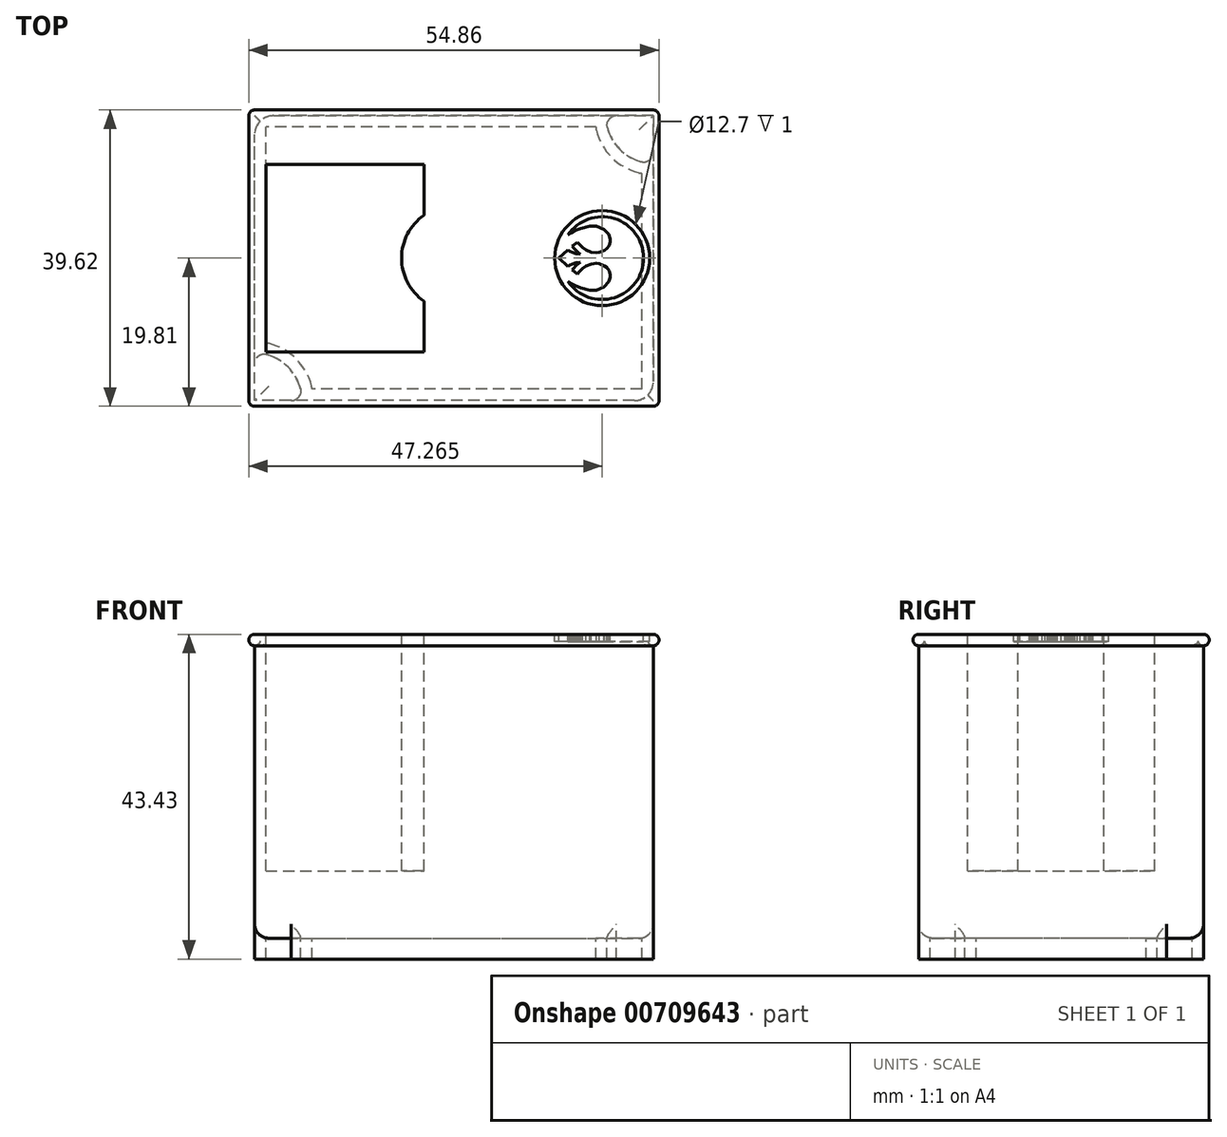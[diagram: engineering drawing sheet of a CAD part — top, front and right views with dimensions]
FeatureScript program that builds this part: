
annotation { "Feature Type Name" : "Feature", "Feature Type Description" : "" }
export const myFeature = defineFeature(function(context is Context, id is Id, definition is map)
    precondition{}
    {
        {
            var Q0;
            Q0=qCreatedBy(makeId("Front.planeOp"),FACE);
            var sketch = newSketch(context, id + "F0", { "sketchPlane" : qUnion([Q0])});
            skLineSegment(sketch, "E0.bottom", {"start": v(26.67, -20.32) * mm, "end": v(-26.67, -20.32) * mm});
            skLineSegment(sketch, "E0.top", {"start": v(26.67, 20.32) * mm, "end": v(-26.67, 20.32) * mm});
            skLineSegment(sketch, "E0.left", {"start": v(26.67, -20.32) * mm, "end": v(26.67, 20.32) * mm});
            skLineSegment(sketch, "E0.right", {"start": v(-26.67, -20.32) * mm, "end": v(-26.67, 20.32) * mm});
            skPoint(sketch, "E0.middle", {"position": v(0, 0) * mm});
            skSolve(sketch);
        }
        {
            var Q0;
            Q0=makeQuery(id+"F0.imprint","IMPRINT",FACE,{"disambiguationData":[TD([[makeQuery(id+"F0.imprint","IMPRINT",EDGE,{"derivedFrom":sQuery(id+"F0.wireOp",EDGE,"E0.bottom")}),-1.0]])]});
            extrude(context, id + "F1", {"entities" : qUnion([Q0]), "depth" : 38.1 * mm, "symmetric" : true});
        }
        {
            var Q0;
            Q0=makeQuery(id+"F1.opExtrude","SWEPT_FACE",FACE,{"disambiguationData":[OSD([sQuery(id+"F0.wireOp",EDGE,"E0.top")])]});
            shell(context, id + "F2", {"entities" : qUnion([Q0]), "thickness" : 1.52 * mm});
        }
        {
            var Q0;
            Q0=makeQuery(id+"F1.opExtrude","CAP_FACE",FACE,{"disambiguationData":[OSD([sQuery(id+"F0.wireOp",EDGE,"E0.bottom"),sQuery(id+"F0.wireOp",EDGE,"E0.top"),sQuery(id+"F0.wireOp",EDGE,"E0.left"),sQuery(id+"F0.wireOp",EDGE,"E0.right")])],"isStart":false});
            var sketch = newSketch(context, id + "F3", { "sketchPlane" : qUnion([Q0])});
            skArc(sketch, "E1", {"start": v(-26.67, 20.32) * mm, "mid": v(-27.43, 19.56) * mm, "end": v(-26.67, 18.8) * mm});
            skSolve(sketch);
        }
        {
            var Q0;
            {var subQ0=sQuery(id+"F3.wireOp",EDGE,"E1");Q0=makeQuery(id+"F3.imprint","IMPRINT",FACE,{"disambiguationData":[TD([[makeQuery(id+"F3.imprint","IMPRINT",EDGE,{"derivedFrom":subQ0}),1.0]])]});}
            var Q1;
            Q1=makeQuery(id+"F1.opExtrude","SWEPT_EDGE",EDGE,{"disambiguationData":[OSD([sQuery(id+"F0.wireOp",EDGE,"E0.top"),sQuery(id+"F0.wireOp",EDGE,"E0.right")])]});
            var Q2;
            Q2=makeQuery(id+"F1.opExtrude","CAP_EDGE",EDGE,{"disambiguationData":[OSD([sQuery(id+"F0.wireOp",EDGE,"E0.top")])],"isStart":true});
            var Q3;
            Q3=makeQuery(id+"F1.opExtrude","SWEPT_EDGE",EDGE,{"disambiguationData":[OSD([sQuery(id+"F0.wireOp",EDGE,"E0.top"),sQuery(id+"F0.wireOp",EDGE,"E0.left")])]});
            var Q4;
            Q4=makeQuery(id+"F1.opExtrude","CAP_EDGE",EDGE,{"disambiguationData":[OSD([sQuery(id+"F0.wireOp",EDGE,"E0.top")])],"isStart":false});
            sweep(context, id + "F4", {"operationType" : NewBodyOperationType.ADD, "profiles" : qUnion([Q0]), "path" : qUnion([Q1, Q2, Q3, Q4])});
        }
        {
            var Q0;
            Q0=makeQuery(id+"F1.opExtrude","SWEPT_FACE",FACE,{"disambiguationData":[OSD([sQuery(id+"F0.wireOp",EDGE,"E0.bottom")])]});
            var sketch = newSketch(context, id + "F5", { "sketchPlane" : qUnion([Q0])});
            skLineSegment(sketch, "E2.bottom", {"start": v(26.67, 19.05) * mm, "end": v(21.75, 19.05) * mm});
            skLineSegment(sketch, "E2.left", {"start": v(26.67, 19.05) * mm, "end": v(26.67, 14.13) * mm});
            skPoint(sketch, "E3.newPointA", {"position": v(20.32, 19.05) * mm});
            skArc(sketch, "E4", {"start": v(20.52, 17.46) * mm, "mid": v(22.18, 14.56) * mm, "end": v(25.08, 12.9) * mm});
            skArc(sketch, "E5.filletArc", {"start": v(21.75, 19.05) * mm, "mid": v(20.75, 18.56) * mm, "end": v(20.52, 17.46) * mm});
            skPoint(sketch, "E6.visualSharp", {"position": v(26.67, 12.7) * mm});
            skArc(sketch, "E6.filletArc", {"start": v(25.08, 12.9) * mm, "mid": v(26.18, 13.13) * mm, "end": v(26.67, 14.13) * mm});
            skArc(sketch, "E7.MirrorCS", {"start": v(-21.75, 19.05) * mm, "mid": v(-20.75, 18.56) * mm, "end": v(-20.52, 17.46) * mm});
            skArc(sketch, "E8.MirrorCS", {"start": v(-20.52, 17.46) * mm, "mid": v(-22.18, 14.56) * mm, "end": v(-25.08, 12.9) * mm});
            skArc(sketch, "E9.MirrorCS", {"start": v(-25.08, 12.9) * mm, "mid": v(-26.18, 13.13) * mm, "end": v(-26.67, 14.13) * mm});
            skLineSegment(sketch, "E10.MirrorCS", {"start": v(-26.67, 19.05) * mm, "end": v(-26.67, 14.13) * mm});
            skLineSegment(sketch, "E11.MirrorCS", {"start": v(-26.67, 19.05) * mm, "end": v(-21.75, 19.05) * mm});
            skArc(sketch, "E12.MirrorCS", {"start": v(-20.52, -17.46) * mm, "mid": v(-22.18, -14.56) * mm, "end": v(-25.08, -12.9) * mm});
            skArc(sketch, "E13.MirrorCS", {"start": v(-21.75, -19.05) * mm, "mid": v(-20.75, -18.56) * mm, "end": v(-20.52, -17.46) * mm});
            skLineSegment(sketch, "E14.MirrorCS", {"start": v(-26.67, -19.05) * mm, "end": v(-21.75, -19.05) * mm});
            skLineSegment(sketch, "E15.MirrorCS", {"start": v(-26.67, -19.05) * mm, "end": v(-26.67, -14.13) * mm});
            skArc(sketch, "E16.MirrorCS", {"start": v(-25.08, -12.9) * mm, "mid": v(-26.18, -13.13) * mm, "end": v(-26.67, -14.13) * mm});
            skArc(sketch, "E17.MirrorCS", {"start": v(21.75, -19.05) * mm, "mid": v(20.75, -18.56) * mm, "end": v(20.52, -17.46) * mm});
            skArc(sketch, "E18.MirrorCS", {"start": v(20.52, -17.46) * mm, "mid": v(22.18, -14.56) * mm, "end": v(25.08, -12.9) * mm});
            skArc(sketch, "E19.MirrorCS", {"start": v(25.08, -12.9) * mm, "mid": v(26.18, -13.13) * mm, "end": v(26.67, -14.13) * mm});
            skLineSegment(sketch, "E20.MirrorCS", {"start": v(26.67, -19.05) * mm, "end": v(26.67, -14.13) * mm});
            skLineSegment(sketch, "E21.MirrorCS", {"start": v(26.67, -19.05) * mm, "end": v(21.75, -19.05) * mm});
            skSolve(sketch);
        }
        {
            var Q0;
            Q0=makeQuery(id+"F5.imprint","IMPRINT",FACE,{"disambiguationData":[TD([[makeQuery(id+"F5.imprint","IMPRINT",EDGE,{"derivedFrom":sQuery(id+"F5.wireOp",EDGE,"E2.bottom")}),1.0]])]});
            var Q1;
            Q1=makeQuery(id+"F5.imprint","IMPRINT",FACE,{"disambiguationData":[TD([[makeQuery(id+"F5.imprint","IMPRINT",EDGE,{"derivedFrom":sQuery(id+"F5.wireOp",EDGE,"E8.MirrorCS")}),-1.0]])]});
            var Q2;
            Q2=makeQuery(id+"F5.imprint","IMPRINT",FACE,{"disambiguationData":[TD([[makeQuery(id+"F5.imprint","IMPRINT",EDGE,{"derivedFrom":sQuery(id+"F5.wireOp",EDGE,"E12.MirrorCS")}),1.0]])]});
            var Q3;
            Q3=makeQuery(id+"F5.imprint","IMPRINT",FACE,{"disambiguationData":[TD([[makeQuery(id+"F5.imprint","IMPRINT",EDGE,{"derivedFrom":sQuery(id+"F5.wireOp",EDGE,"E17.MirrorCS")}),-1.0]])]});
            extrude(context, id + "F6", {"entities" : qUnion([Q0, Q1, Q2, Q3]), "operationType" : NewBodyOperationType.ADD, "depth" : 2.8 * mm});
        }
        {
            var Q0;
            Q0=makeQuery(id+"F6.opExtrude","CAP_FACE",FACE,{"disambiguationData":[OSD([sQuery(id+"F5.wireOp",EDGE,"E2.bottom"),sQuery(id+"F5.wireOp",EDGE,"E2.left"),sQuery(id+"F5.wireOp",EDGE,"E4"),sQuery(id+"F5.wireOp",EDGE,"E5.filletArc"),sQuery(id+"F5.wireOp",EDGE,"E6.filletArc")])],"isStart":false});
            var Q1;
            Q1=makeQuery(id+"F6.opExtrude","CAP_FACE",FACE,{"disambiguationData":[OSD([sQuery(id+"F5.wireOp",EDGE,"E8.MirrorCS"),sQuery(id+"F5.wireOp",EDGE,"E9.MirrorCS"),sQuery(id+"F5.wireOp",EDGE,"E10.MirrorCS"),sQuery(id+"F5.wireOp",EDGE,"E7.MirrorCS"),sQuery(id+"F5.wireOp",EDGE,"E11.MirrorCS")])],"isStart":false});
            var Q2;
            Q2=makeQuery(id+"F6.opExtrude","CAP_FACE",FACE,{"disambiguationData":[OSD([sQuery(id+"F5.wireOp",EDGE,"E12.MirrorCS"),sQuery(id+"F5.wireOp",EDGE,"E13.MirrorCS"),sQuery(id+"F5.wireOp",EDGE,"E14.MirrorCS"),sQuery(id+"F5.wireOp",EDGE,"E15.MirrorCS"),sQuery(id+"F5.wireOp",EDGE,"E16.MirrorCS")])],"isStart":false});
            var Q3;
            Q3=makeQuery(id+"F6.opExtrude","CAP_FACE",FACE,{"disambiguationData":[OSD([sQuery(id+"F5.wireOp",EDGE,"E17.MirrorCS"),sQuery(id+"F5.wireOp",EDGE,"E18.MirrorCS"),sQuery(id+"F5.wireOp",EDGE,"E19.MirrorCS"),sQuery(id+"F5.wireOp",EDGE,"E20.MirrorCS"),sQuery(id+"F5.wireOp",EDGE,"E21.MirrorCS")])],"isStart":false});
            shell(context, id + "F7", {"entities" : qUnion([Q0, Q1, Q2, Q3]), "thickness" : 1.52 * mm});
        }
        {
            var Q0;
            Q0=makeQuery(id+"F2.opShell","OFFSET_FACE",FACE,{"disambiguationData":[OSD([sQuery(id+"F0.wireOp",EDGE,"E0.bottom")])]});
            extrude(context, id + "F8", {"entities" : qUnion([Q0]), "operationType" : NewBodyOperationType.ADD, "surfaceOperationType" : NewSurfaceOperationType.ADD, "depth" : 7.5 * mm, "offsetDistance" : 25 * mm});
        }
        {
            var Q0;
            Q0=makeQuery(id+"F1.opExtrude","SWEPT_EDGE",EDGE,{"disambiguationData":[OSD([sQuery(id+"F0.wireOp",EDGE,"E0.bottom"),sQuery(id+"F0.wireOp",EDGE,"E0.right")])]});
            var Q1;
            Q1=makeQuery(id+"F1.opExtrude","CAP_EDGE",EDGE,{"disambiguationData":[OSD([sQuery(id+"F0.wireOp",EDGE,"E0.bottom")])],"isStart":false});
            var Q2;
            Q2=makeQuery(id+"F1.opExtrude","SWEPT_EDGE",EDGE,{"disambiguationData":[OSD([sQuery(id+"F0.wireOp",EDGE,"E0.bottom"),sQuery(id+"F0.wireOp",EDGE,"E0.left")])]});
            var Q3;
            Q3=makeQuery(id+"F1.opExtrude","CAP_EDGE",EDGE,{"disambiguationData":[OSD([sQuery(id+"F0.wireOp",EDGE,"E0.bottom")])],"isStart":true});
            fillet(context, id + "F9", {"entities" : qUnion([Q0, Q1, Q2, Q3]), "radius" : 1.9 * mm, "tangentPropagation" : true, "allowEdgeOverflow" : false});
        }
        {
            var Q0;
            Q0=makeQuery(id+"F4.opSweep","MID_CAP_EDGE",EDGE,{"disambiguationData":[OSD([sQuery(id+"F0.wireOp",EDGE,"E0.top"),sQuery(id+"F0.wireOp",EDGE,"E0.left"),sQuery(id+"F3.wireOp",EDGE,"E1")])],"capPos":3.0});
            var Q1;
            Q1=makeQuery(id+"F4.opSweep","MID_CAP_EDGE",EDGE,{"disambiguationData":[OSD([sQuery(id+"F0.wireOp",EDGE,"E0.top"),sQuery(id+"F0.wireOp",EDGE,"E0.left"),sQuery(id+"F3.wireOp",EDGE,"E1")])],"capPos":2.0});
            var Q2;
            Q2=makeQuery(id+"F4.opSweep","MID_CAP_EDGE",EDGE,{"disambiguationData":[OSD([sQuery(id+"F0.wireOp",EDGE,"E0.top"),sQuery(id+"F0.wireOp",EDGE,"E0.right"),sQuery(id+"F3.wireOp",EDGE,"E1")])],"capPos":1.0});
            var Q3;
            Q3=makeQuery(id+"F4.opSweep","CAP_EDGE",EDGE,{"disambiguationData":[OSD([sQuery(id+"F0.wireOp",EDGE,"E0.top"),sQuery(id+"F0.wireOp",EDGE,"E0.right"),sQuery(id+"F3.wireOp",EDGE,"E1")])],"isStart":true});
            fillet(context, id + "F10", {"entities" : qUnion([Q0, Q1, Q2, Q3]), "radius" : 0.76 * mm, "tangentPropagation" : true, "allowEdgeOverflow" : false});
        }
        {
            var Q0;
            Q0=makeQuery(id+"F6.boolean.opBoolean","MERGE",EDGE,{"derivedFrom":[makeQuery(id+"F1.opExtrude","CAP_EDGE",EDGE,{"disambiguationData":[OSD([sQuery(id+"F0.wireOp",EDGE,"E0.left")])],"isStart":false}),makeQuery(id+"F6.opExtrude","SWEPT_EDGE",EDGE,{"disambiguationData":[OSD([sQuery(id+"F5.wireOp",EDGE,"E2.bottom"),sQuery(id+"F5.wireOp",EDGE,"E2.left")])]})]});
            var Q1;
            Q1=makeQuery(id+"F6.boolean.opBoolean","MERGE",EDGE,{"derivedFrom":[makeQuery(id+"F1.opExtrude","CAP_EDGE",EDGE,{"disambiguationData":[OSD([sQuery(id+"F0.wireOp",EDGE,"E0.left")])],"isStart":true}),makeQuery(id+"F6.opExtrude","SWEPT_EDGE",EDGE,{"disambiguationData":[OSD([sQuery(id+"F5.wireOp",EDGE,"E20.MirrorCS"),sQuery(id+"F5.wireOp",EDGE,"E21.MirrorCS")])]})]});
            var Q2;
            Q2=makeQuery(id+"F6.boolean.opBoolean","MERGE",EDGE,{"derivedFrom":[makeQuery(id+"F1.opExtrude","CAP_EDGE",EDGE,{"disambiguationData":[OSD([sQuery(id+"F0.wireOp",EDGE,"E0.right")])],"isStart":false}),makeQuery(id+"F6.opExtrude","SWEPT_EDGE",EDGE,{"disambiguationData":[OSD([sQuery(id+"F5.wireOp",EDGE,"E10.MirrorCS"),sQuery(id+"F5.wireOp",EDGE,"E11.MirrorCS")])]})]});
            var Q3;
            Q3=makeQuery(id+"F6.boolean.opBoolean","MERGE",EDGE,{"derivedFrom":[makeQuery(id+"F1.opExtrude","CAP_EDGE",EDGE,{"disambiguationData":[OSD([sQuery(id+"F0.wireOp",EDGE,"E0.right")])],"isStart":true}),makeQuery(id+"F6.opExtrude","SWEPT_EDGE",EDGE,{"disambiguationData":[OSD([sQuery(id+"F5.wireOp",EDGE,"E14.MirrorCS"),sQuery(id+"F5.wireOp",EDGE,"E15.MirrorCS")])]})]});
            fillet(context, id + "F11", {"entities" : qUnion([Q0, Q1, Q2, Q3]), "radius" : 2.54 * mm, "tangentPropagation" : true, "allowEdgeOverflow" : false});
        }
        {
            var Q0;
            Q0=makeQuery(id+"F1.opExtrude","SWEPT_FACE",FACE,{"disambiguationData":[OSD([sQuery(id+"F0.wireOp",EDGE,"E0.top")])]});
            var sketch = newSketch(context, id + "F12", { "sketchPlane" : qUnion([Q0])});
            skLineSegment(sketch, "E22.0", {"start": v(25.15, -17.53) * mm, "end": v(-25.15, -17.53) * mm});
            skLineSegment(sketch, "E22.1", {"start": v(-25.15, -17.53) * mm, "end": v(-25.15, 17.53) * mm});
            skLineSegment(sketch, "E22.2", {"start": v(25.15, 17.53) * mm, "end": v(-25.15, 17.53) * mm});
            skLineSegment(sketch, "E22.3", {"start": v(25.15, -17.53) * mm, "end": v(25.15, 17.53) * mm});
            skLineSegment(sketch, "E23", {"start": v(-25.15, 17.53) * mm, "end": v(-25.15, 12.53) * mm});
            skLineSegment(sketch, "E24", {"start": v(-25.15, 12.53) * mm, "end": v(-4, 12.53) * mm});
            skLineSegment(sketch, "E25", {"start": v(-25.15, -17.53) * mm, "end": v(-25.15, -12.53) * mm});
            skLineSegment(sketch, "E26", {"start": v(-25.15, -12.53) * mm, "end": v(-4, -12.53) * mm});
            skLineSegment(sketch, "E27.left", {"start": v(-4, 12.53) * mm, "end": v(-4, 5.74) * mm});
            skLineSegment(sketch, "E27.right", {"start": v(4, 12.53) * mm, "end": v(4, 5.74) * mm});
            skPoint(sketch, "E27.middle", {"position": v(0, 0) * mm});
            skArc(sketch, "E28", {"start": v(-4, 5.74) * mm, "mid": v(-7, 0) * mm, "end": v(-4, -5.74) * mm});
            skLineSegment(sketch, "E29.bottom", {"start": v(13, 2.25) * mm, "end": v(6.63, 2.25) * mm});
            skLineSegment(sketch, "E29.top", {"start": v(13, -2.25) * mm, "end": v(6.63, -2.25) * mm});
            skLineSegment(sketch, "E29.left", {"start": v(13, 2.25) * mm, "end": v(13, -2.25) * mm});
            skLineSegment(sketch, "E30.trimOffspring", {"start": v(4, -5.74) * mm, "end": v(4, -12.53) * mm});
            skLineSegment(sketch, "E31.trimOffspring", {"start": v(-4, -5.74) * mm, "end": v(-4, -12.53) * mm});
            skArc(sketch, "E32.trimOffspring", {"start": v(4, -5.74) * mm, "mid": v(5.6, -4.2) * mm, "end": v(6.63, -2.25) * mm});
            skLineSegment(sketch, "E33.trimOffspring", {"start": v(4, -12.53) * mm, "end": v(25.15, -12.53) * mm});
            skLineSegment(sketch, "E34.trimOffspring", {"start": v(4, 12.53) * mm, "end": v(25.15, 12.53) * mm});
            skArc(sketch, "E35.trimOffspring", {"start": v(6.63, 2.25) * mm, "mid": v(5.6, 4.2) * mm, "end": v(4, 5.74) * mm});
            skSolve(sketch);
        }
        {
            var Q0;
            Q0=makeQuery(id+"F12.imprint","IMPRINT",FACE,{"disambiguationData":[TD([[makeQuery(id+"F12.imprint","IMPRINT",EDGE,{"derivedFrom":sQuery(id+"F12.wireOp",EDGE,"E22.1")}),-1.0]])]});
            var Q1;
            Q1=makeQuery(id+"F12.imprint","IMPRINT",FACE,{"disambiguationData":[TD([[makeQuery(id+"F12.imprint","IMPRINT",EDGE,{"derivedFrom":sQuery(id+"F12.wireOp",EDGE,"E27.right")}),1.0]])]});
            var Q2;
            Q2=makeQuery(id+"F8.opExtrude","CAP_FACE",FACE,{"disambiguationData":[OSD([sQuery(id+"F0.wireOp",EDGE,"E0.bottom")])],"isStart":false});
            extrude(context, id + "F13", {"entities" : qUnion([Q0, Q1]), "operationType" : NewBodyOperationType.ADD, "endBound" : BoundingType.UP_TO_SURFACE, "oppositeDirection" : true, "depth" : 25 * mm, "endBoundEntityFace" : qUnion([Q2]), "offsetDistance" : 25 * mm});
        }
        {
            var Q0;
            {var subQ2=sQuery(id+"F0.wireOp",EDGE,"E0.top");var subQ4=sQuery(id+"F12.wireOp",EDGE,"E30.trimOffspring");var subQ5=sQuery(id+"F12.wireOp",EDGE,"E27.left");var subQ6=sQuery(id+"F0.wireOp",EDGE,"E0.left");var subQ7=sQuery(id+"F12.wireOp",EDGE,"E24");var subQ8=sQuery(id+"F12.wireOp",EDGE,"E26");var subQ9=sQuery(id+"F12.wireOp",EDGE,"E29.bottom");var subQ11=sQuery(id+"F12.wireOp",EDGE,"E28");var subQ12=sQuery(id+"F12.wireOp",EDGE,"E27.right");var subQ13=sQuery(id+"F12.wireOp",EDGE,"E29.left");var subQ14=sQuery(id+"F12.wireOp",EDGE,"E31.trimOffspring");var subQ15=sQuery(id+"F12.wireOp",EDGE,"E29.top");var subQ16=sQuery(id+"F12.wireOp",EDGE,"E32.trimOffspring");var subQ17=sQuery(id+"F12.wireOp",EDGE,"E33.trimOffspring");var subQ18=sQuery(id+"F12.wireOp",EDGE,"E34.trimOffspring");var subQ19=sQuery(id+"F12.wireOp",EDGE,"E35.trimOffspring");Q0=makeQuery(id+"F16.boolean.opBoolean","SPLIT",FACE,{"disambiguationData":[TD([makeQuery(id+"F2.opShell","OFFSET_FACE",FACE,{"disambiguationData":[OSD([subQ6])]})])],"derivedFrom":makeQuery(id+"F13.boolean.opBoolean","MERGE",FACE,{"derivedFrom":[makeQuery(id+"F1.opExtrude","SWEPT_FACE",FACE,{"disambiguationData":[OSD([subQ2])]}),makeQuery(id+"F13.opExtrude","CAP_FACE",FACE,{"disambiguationData":[OSD([sQuery(id+"F12.wireOp",EDGE,"E22.1"),subQ7,subQ8,subQ5,subQ11,subQ14])],"isStart":true}),makeQuery(id+"F13.opExtrude","CAP_FACE",FACE,{"disambiguationData":[OSD([sQuery(id+"F12.wireOp",EDGE,"E22.3"),subQ12,subQ9,subQ15,subQ13,subQ4,subQ16,subQ17,subQ18,subQ19])],"isStart":true})]})});}
            var sketch = newSketch(context, id + "F14", { "sketchPlane" : qUnion([Q0])});
            skCircle(sketch, "E36", {"center": v(19.84, 0) * mm, "radius": 6.35 * mm});
            skLineSegment(sketch, "E37", {"start": v(15.28, 1.1) * mm, "end": v(14.03, 0) * mm});
            skLineSegment(sketch, "E38", {"start": v(15.83, 1.6) * mm, "end": v(16.54, 2.14) * mm});
            skLineSegment(sketch, "E39", {"start": v(16.54, 2.14) * mm, "end": v(16.77, 1.84) * mm});
            skLineSegment(sketch, "E40", {"start": v(16.77, 1.84) * mm, "end": v(17.23, 1.4) * mm});
            skLineSegment(sketch, "E41", {"start": v(17.23, 1.4) * mm, "end": v(17.63, 1.08) * mm});
            skLineSegment(sketch, "E42", {"start": v(17.63, 1.08) * mm, "end": v(18.33, 0.77) * mm});
            skLineSegment(sketch, "E43", {"start": v(18.33, 0.77) * mm, "end": v(19.08, 0.7) * mm});
            skLineSegment(sketch, "E44", {"start": v(19.08, 0.7) * mm, "end": v(19.45, 0.76) * mm});
            skLineSegment(sketch, "E45", {"start": v(19.45, 0.76) * mm, "end": v(20.14, 1.07) * mm});
            skLineSegment(sketch, "E46", {"start": v(20.14, 1.07) * mm, "end": v(20.46, 1.27) * mm});
            skLineSegment(sketch, "E47", {"start": v(20.46, 1.27) * mm, "end": v(20.75, 1.7) * mm});
            skLineSegment(sketch, "E48", {"start": v(20.75, 1.7) * mm, "end": v(20.9, 2.19) * mm});
            skLineSegment(sketch, "E49", {"start": v(20.9, 2.19) * mm, "end": v(20.9, 2.56) * mm});
            skLineSegment(sketch, "E50", {"start": v(20.9, 2.56) * mm, "end": v(20.71, 3.18) * mm});
            skLineSegment(sketch, "E51", {"start": v(20.71, 3.18) * mm, "end": v(20.1, 3.83) * mm});
            skLineSegment(sketch, "E52", {"start": v(20.1, 3.83) * mm, "end": v(19.06, 4.28) * mm});
            skLineSegment(sketch, "E53", {"start": v(19.06, 4.28) * mm, "end": v(18.18, 4.28) * mm});
            skLineSegment(sketch, "E54", {"start": v(18.18, 4.28) * mm, "end": v(16.93, 3.99) * mm});
            skLineSegment(sketch, "E55", {"start": v(16.93, 3.99) * mm, "end": v(16.22, 3.69) * mm});
            skLineSegment(sketch, "E56", {"start": v(16.22, 3.69) * mm, "end": v(15.67, 3.4) * mm});
            skLineSegment(sketch, "E57", {"start": v(15.67, 3.4) * mm, "end": v(15.26, 3.1) * mm});
            skLineSegment(sketch, "E58", {"start": v(15.83, 1.6) * mm, "end": v(16, 1.38) * mm});
            skLineSegment(sketch, "E59", {"start": v(16, 1.38) * mm, "end": v(16.35, 1.02) * mm});
            skLineSegment(sketch, "E60", {"start": v(16.35, 1.02) * mm, "end": v(16.62, 0.74) * mm});
            skLineSegment(sketch, "E61", {"start": v(16.62, 0.74) * mm, "end": v(16.93, 0.53) * mm});
            skLineSegment(sketch, "E62", {"start": v(16.93, 0.53) * mm, "end": v(16.3, 0.62) * mm});
            skLineSegment(sketch, "E63", {"start": v(16.3, 0.62) * mm, "end": v(15.83, 0.78) * mm});
            skLineSegment(sketch, "E64", {"start": v(15.83, 0.78) * mm, "end": v(15.49, 0.93) * mm});
            skLineSegment(sketch, "E65", {"start": v(15.49, 0.93) * mm, "end": v(15.28, 1.1) * mm});
            skPoint(sketch, "E66.start.orphan", {"position": v(13.49, 0) * mm});
            skLineSegment(sketch, "E67.MirrorCS", {"start": v(20.46, -1.27) * mm, "end": v(20.75, -1.7) * mm});
            skLineSegment(sketch, "E68.MirrorCS", {"start": v(16.22, -3.69) * mm, "end": v(15.67, -3.4) * mm});
            skLineSegment(sketch, "E69.MirrorCS", {"start": v(20.14, -1.07) * mm, "end": v(20.46, -1.27) * mm});
            skLineSegment(sketch, "E70.MirrorCS", {"start": v(19.06, -4.28) * mm, "end": v(18.18, -4.28) * mm});
            skLineSegment(sketch, "E71.MirrorCS", {"start": v(16.93, -0.53) * mm, "end": v(16.3, -0.62) * mm});
            skLineSegment(sketch, "E72.MirrorCS", {"start": v(16.77, -1.84) * mm, "end": v(17.23, -1.4) * mm});
            skLineSegment(sketch, "E73.MirrorCS", {"start": v(16.3, -0.62) * mm, "end": v(15.83, -0.78) * mm});
            skLineSegment(sketch, "E74.MirrorCS", {"start": v(15.83, -0.78) * mm, "end": v(15.49, -0.93) * mm});
            skLineSegment(sketch, "E75.MirrorCS", {"start": v(16.62, -0.74) * mm, "end": v(16.93, -0.53) * mm});
            skLineSegment(sketch, "E76.MirrorCS", {"start": v(20.9, -2.56) * mm, "end": v(20.71, -3.18) * mm});
            skLineSegment(sketch, "E77.MirrorCS", {"start": v(20.71, -3.18) * mm, "end": v(20.1, -3.83) * mm});
            skLineSegment(sketch, "E78.MirrorCS", {"start": v(15.67, -3.4) * mm, "end": v(15.26, -3.1) * mm});
            skLineSegment(sketch, "E79.MirrorCS", {"start": v(16.93, -3.99) * mm, "end": v(16.22, -3.69) * mm});
            skLineSegment(sketch, "E80.MirrorCS", {"start": v(16, -1.38) * mm, "end": v(16.35, -1.02) * mm});
            skLineSegment(sketch, "E81.MirrorCS", {"start": v(17.23, -1.4) * mm, "end": v(17.63, -1.08) * mm});
            skLineSegment(sketch, "E82.MirrorCS", {"start": v(20.75, -1.7) * mm, "end": v(20.9, -2.19) * mm});
            skLineSegment(sketch, "E83.MirrorCS", {"start": v(16.54, -2.14) * mm, "end": v(16.77, -1.84) * mm});
            skLineSegment(sketch, "E84.MirrorCS", {"start": v(15.83, -1.6) * mm, "end": v(16, -1.38) * mm});
            skLineSegment(sketch, "E85.MirrorCS", {"start": v(19.45, -0.76) * mm, "end": v(20.14, -1.07) * mm});
            skLineSegment(sketch, "E86.MirrorCS", {"start": v(15.83, -1.6) * mm, "end": v(16.54, -2.14) * mm});
            skLineSegment(sketch, "E87.MirrorCS", {"start": v(19.08, -0.7) * mm, "end": v(19.45, -0.76) * mm});
            skLineSegment(sketch, "E88.MirrorCS", {"start": v(17.63, -1.08) * mm, "end": v(18.33, -0.77) * mm});
            skLineSegment(sketch, "E89.MirrorCS", {"start": v(18.33, -0.77) * mm, "end": v(19.08, -0.7) * mm});
            skLineSegment(sketch, "E90.MirrorCS", {"start": v(16.35, -1.02) * mm, "end": v(16.62, -0.74) * mm});
            skLineSegment(sketch, "E91.MirrorCS", {"start": v(15.49, -0.93) * mm, "end": v(15.28, -1.1) * mm});
            skLineSegment(sketch, "E92.MirrorCS", {"start": v(20.9, -2.19) * mm, "end": v(20.9, -2.56) * mm});
            skLineSegment(sketch, "E93.MirrorCS", {"start": v(18.18, -4.28) * mm, "end": v(16.93, -3.99) * mm});
            skLineSegment(sketch, "E94.MirrorCS", {"start": v(15.28, -1.1) * mm, "end": v(14.03, 0) * mm});
            skLineSegment(sketch, "E95.MirrorCS", {"start": v(20.1, -3.83) * mm, "end": v(19.06, -4.28) * mm});
            skArc(sketch, "E96", {"start": v(15.26, -3.1) * mm, "mid": v(25.37, 0) * mm, "end": v(15.26, 3.1) * mm});
            skPoint(sketch, "E97", {"position": v(19.83, 0) * mm});
            skPoint(sketch, "E98", {"position": v(19.84, 6.35) * mm});
            skPoint(sketch, "E99.0", {"position": v(13, 0) * mm});
            skPoint(sketch, "E100.0", {"position": v(26.67, 0) * mm});
            skSolve(sketch);
        }
        {
            var Q0;
            Q0=makeQuery(id+"F13.boolean.opBoolean","MERGE",FACE,{"derivedFrom":[makeQuery(id+"F1.opExtrude","SWEPT_FACE",FACE,{"disambiguationData":[OSD([sQuery(id+"F0.wireOp",EDGE,"E0.top")])]}),makeQuery(id+"F13.opExtrude","CAP_FACE",FACE,{"disambiguationData":[OSD([sQuery(id+"F12.wireOp",EDGE,"E22.1"),sQuery(id+"F12.wireOp",EDGE,"E24"),sQuery(id+"F12.wireOp",EDGE,"E26"),sQuery(id+"F12.wireOp",EDGE,"E27.left"),sQuery(id+"F12.wireOp",EDGE,"E28"),sQuery(id+"F12.wireOp",EDGE,"E31.trimOffspring")])],"isStart":true}),makeQuery(id+"F13.opExtrude","CAP_FACE",FACE,{"disambiguationData":[OSD([sQuery(id+"F12.wireOp",EDGE,"E22.3"),sQuery(id+"F12.wireOp",EDGE,"E27.right"),sQuery(id+"F12.wireOp",EDGE,"E29.bottom"),sQuery(id+"F12.wireOp",EDGE,"E29.top"),sQuery(id+"F12.wireOp",EDGE,"E29.left"),sQuery(id+"F12.wireOp",EDGE,"E30.trimOffspring"),sQuery(id+"F12.wireOp",EDGE,"E32.trimOffspring"),sQuery(id+"F12.wireOp",EDGE,"E33.trimOffspring"),sQuery(id+"F12.wireOp",EDGE,"E34.trimOffspring"),sQuery(id+"F12.wireOp",EDGE,"E35.trimOffspring")])],"isStart":true})]});
            var sketch = newSketch(context, id + "F15", { "sketchPlane" : qUnion([Q0])});
            skPoint(sketch, "E101.0", {"position": v(-22.16, -12.53) * mm});
            skPoint(sketch, "E102", {"position": v(-18.34, -11.53) * mm});
            skLineSegment(sketch, "E103", {"start": v(-13.8, 0) * mm, "end": v(-12.37, 0) * mm});
            skPoint(sketch, "E104", {"position": v(-12.37, -11.53) * mm});
            skPoint(sketch, "E105", {"position": v(-12.37, 11.53) * mm});
            skPoint(sketch, "E106", {"position": v(-13.8, 11.53) * mm});
            skPoint(sketch, "E107", {"position": v(-13.8, -11.53) * mm});
            skPoint(sketch, "E108", {"position": v(-18.34, 11.53) * mm});
            skPoint(sketch, "E109", {"position": v(-7.84, -11.53) * mm});
            skPoint(sketch, "E110", {"position": v(-7.84, 11.53) * mm});
            skText(sketch, "E111", { "text": "Fighter", "fontName": "NotoSans-Bold.ttf"});
            skPoint(sketch, "E112", {"position": v(-18.34, 0) * mm});
            skText(sketch, "E113", { "text": "TIE", "fontName": "NotoSans-Bold.ttf"});
            skPoint(sketch, "E114.0", {"position": v(-4, 12.53) * mm});
            skLineSegment(sketch, "E115.0", {"start": v(-25.15, 12.53) * mm, "end": v(-7, 12.53) * mm});
            skPoint(sketch, "E116.0", {"position": v(-4.02, 0) * mm});
            skPoint(sketch, "E117.0", {"position": v(-22.37, 50.53) * mm});
            skPoint(sketch, "E118.0", {"position": v(-19.55, 75.58) * mm});
            skPoint(sketch, "E119", {"position": v(-18.55, 51.53) * mm});
            skLineSegment(sketch, "E120", {"start": v(-14.02, 63.06) * mm, "end": v(-12.58, 63.06) * mm});
            skPoint(sketch, "E121", {"position": v(-12.58, 51.53) * mm});
            skPoint(sketch, "E122", {"position": v(-12.58, 74.58) * mm});
            skPoint(sketch, "E123", {"position": v(-14.02, 74.58) * mm});
            skPoint(sketch, "E124", {"position": v(-14.02, 51.53) * mm});
            skPoint(sketch, "E125", {"position": v(-18.55, 74.58) * mm});
            skPoint(sketch, "E126", {"position": v(-8.05, 51.53) * mm});
            skPoint(sketch, "E127", {"position": v(-8.05, 74.58) * mm});
            skText(sketch, "E128", { "text": "Fighter", "fontName": "NotoSans-Bold.ttf"});
            skPoint(sketch, "E129", {"position": v(-18.55, 63.06) * mm});
            skText(sketch, "E130", { "text": "TIE", "fontName": "NotoSans-Bold.ttf"});
            skPoint(sketch, "E131.0", {"position": v(-1.23, 75.58) * mm});
            skLineSegment(sketch, "E132.0", {"start": v(-22.37, 75.58) * mm, "end": v(-4.23, 75.58) * mm});
            skPoint(sketch, "E133.0", {"position": v(-4.23, 63.06) * mm});
            skPoint(sketch, "E134", {"position": v(-24.3, -11.53) * mm});
            skLineSegment(sketch, "E135", {"start": v(-19.78, 0) * mm, "end": v(-18.34, 0) * mm});
            skPoint(sketch, "E136", {"position": v(-24.27, 11.53) * mm});
            skPoint(sketch, "E137", {"position": v(-19.78, -11.53) * mm});
            skPoint(sketch, "E138", {"position": v(-19.78, 11.53) * mm});
            skPoint(sketch, "E139", {"position": v(-24.27, 0) * mm});
            skText(sketch, "E140", { "text": "Sabine\'s", "fontName": "NotoSans-Bold.ttf"});
            skText(sketch, "E141", { "text": "Sabine\'s", "fontName": "NotoSans-Bold.ttf"});
            const initialGuessF15  = {"E111": [-0.00784, -0.01153, 0, 1, 0.00453], "E113": [-0.01381, -0.00482, 0, 1, 0.00452], "E128": [-0.00805, 0.05153, 0, 1, 0.00453], "E130": [-0.01403, 0.05824, 0, 1, 0.00452], "E140": [-0.02958, -0.01255, 0, 1, 0.0044], "E141": [-0.01978, -0.01206, 0, 1, 0.0042]};
            skSetInitialGuess(sketch, initialGuessF15);
            skSolve(sketch);
        }
        {
            var Q0;
            Q0 = qSketchRegion(id + "F15", true);
            var Q1;
            Q1=makeQuery(id+"F14.imprint","IMPRINT",FACE,{"disambiguationData":[TD([[makeQuery(id+"F14.imprint","IMPRINT",EDGE,{"derivedFrom":sQuery(id+"F14.wireOp",EDGE,"E36")}),1.0]])]});
            extrude(context, id + "F16", {"entities" : qUnion([Q0, Q1]), "operationType" : NewBodyOperationType.REMOVE, "oppositeDirection" : true, "depth" : 1 * mm, "offsetDistance" : 25 * mm});
        }
    });
